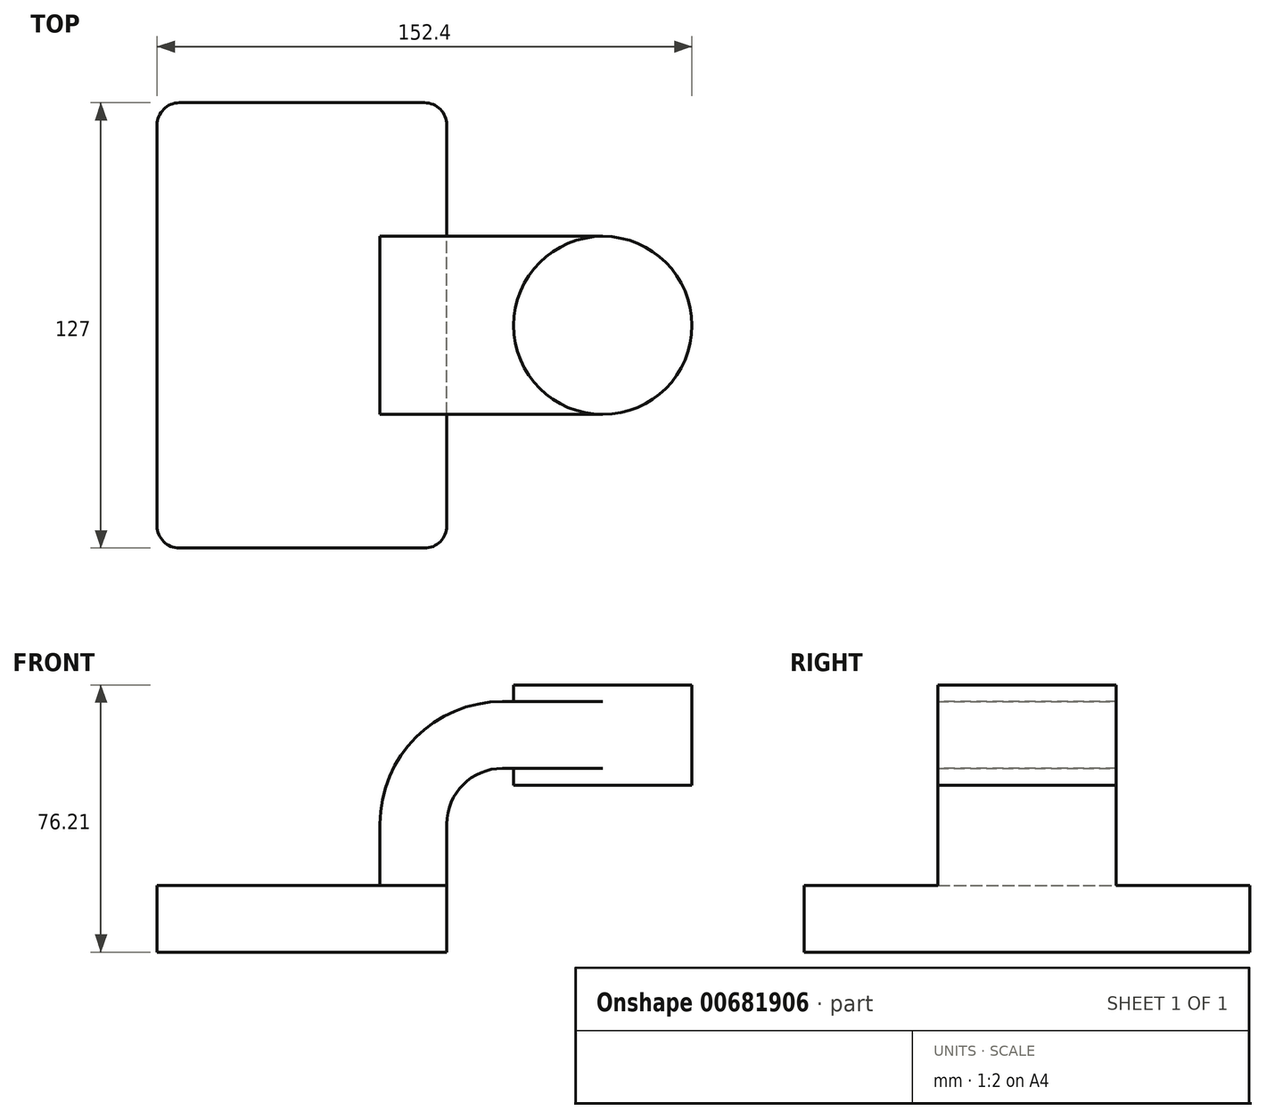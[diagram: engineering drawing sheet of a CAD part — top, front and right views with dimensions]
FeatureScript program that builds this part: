
annotation { "Feature Type Name" : "Feature", "Feature Type Description" : "" }
export const myFeature = defineFeature(function(context is Context, id is Id, definition is map)
    precondition{}
    {
        {
            var Q0;
            Q0=qCreatedBy(makeId("Front.planeOp"),FACE);
            var sketch = newSketch(context, id + "F0", { "sketchPlane" : qUnion([Q0])});
            skLineSegment(sketch, "E0.bottom", {"start": v(-41.28, 9.52) * mm, "end": v(41.27, 9.53) * mm});
            skLineSegment(sketch, "E0.top", {"start": v(-41.28, -9.53) * mm, "end": v(41.28, -9.53) * mm});
            skLineSegment(sketch, "E0.left", {"start": v(-41.28, 9.52) * mm, "end": v(-41.28, -9.53) * mm});
            skLineSegment(sketch, "E0.right", {"start": v(41.27, 9.53) * mm, "end": v(41.28, -9.52) * mm});
            skPoint(sketch, "E0.middle", {"position": v(0, 0) * mm});
            skLineSegment(sketch, "E1.bottom", {"start": v(60.32, 38.1) * mm, "end": v(111.12, 38.1) * mm});
            skLineSegment(sketch, "E1.top", {"start": v(60.32, 66.68) * mm, "end": v(111.12, 66.68) * mm});
            skLineSegment(sketch, "E1.left", {"start": v(60.32, 38.1) * mm, "end": v(60.32, 66.68) * mm});
            skLineSegment(sketch, "E1.right", {"start": v(111.12, 38.1) * mm, "end": v(111.12, 66.68) * mm});
            skPoint(sketch, "E1.middle", {"position": v(85.72, 52.39) * mm});
            skLineSegment(sketch, "E2", {"start": v(41.27, 9.53) * mm, "end": v(41.27, 27) * mm});
            skArc(sketch, "E3", {"start": v(41.27, 27) * mm, "mid": v(45.92, 38.23) * mm, "end": v(57.15, 42.88) * mm});
            skLineSegment(sketch, "E4", {"start": v(57.15, 42.88) * mm, "end": v(85.73, 42.88) * mm});
            skLineSegment(sketch, "E5.0", {"start": v(57.15, 61.93) * mm, "end": v(85.73, 61.93) * mm});
            skArc(sketch, "E5.1", {"start": v(22.22, 27) * mm, "mid": v(32.45, 51.7) * mm, "end": v(57.15, 61.93) * mm});
            skLineSegment(sketch, "E5.2", {"start": v(22.22, 9.53) * mm, "end": v(22.22, 27) * mm});
            skLineSegment(sketch, "E6", {"start": v(85.73, 66.68) * mm, "end": v(85.73, 38.1) * mm});
            skFitSpline(sketch, "E7", {"points": [v(-41.28, 9.53) * mm, v(57.15, 61.93) * mm], "startDerivative": vector(2.17, 103.8) * mm, "endDerivative": vector(152.8, -3.63) * mm});
            skSolve(sketch);
        }
        {
            var Q0;
            Q0=makeQuery(id+"F0.imprint","IMPRINT",FACE,{"disambiguationData":[TD([[makeQuery(id+"F0.imprint","IMPRINT",EDGE,{"derivedFrom":sQuery(id+"F0.wireOp",EDGE,"E0.top")}),1.0]])]});
            extrude(context, id + "F1", {"entities" : qUnion([Q0]), "depth" : 127 * mm, "offsetDistance" : 25.4 * mm, "symmetric" : true});
        }
        {
            var Q0;
            {var subQ1=sQuery(id+"F0.wireOp",EDGE,"E2");Q0=makeQuery(id+"F0.imprint","IMPRINT",FACE,{"disambiguationData":[TD([[makeQuery(id+"F0.imprint","IMPRINT",EDGE,{"derivedFrom":subQ1}),1.0]])]});}
            var Q1;
            {var subQ0=sQuery(id+"F0.wireOp",EDGE,"E4");var subQ1=sQuery(id+"F0.wireOp",EDGE,"E1.left");var subQ2=makeQuery(id+"F0.imprint","INTERSECT",VERTEX,{"derivedFrom":[subQ1,subQ0]});Q1=makeQuery(id+"F0.imprint","IMPRINT",FACE,{"disambiguationData":[TD([[makeQuery(id+"F0.imprint","IMPRINT",EDGE,{"disambiguationData":[TD([[subQ2,-1.0]])],"derivedFrom":subQ1}),-1.0]])]});}
            extrude(context, id + "F2", {"entities" : qUnion([Q0, Q1]), "operationType" : NewBodyOperationType.ADD, "depth" : 50.8 * mm, "offsetDistance" : 25.4 * mm, "symmetric" : true});
        }
        {
            var Q0;
            Q0=makeQuery(id+"F0.imprint","IMPRINT",FACE,{"disambiguationData":[TD([[makeQuery(id+"F0.imprint","IMPRINT",EDGE,{"derivedFrom":sQuery(id+"F0.wireOp",EDGE,"E5.1")}),1.0]])]});
            extrude(context, id + "F3", {"entities" : qUnion([Q0]), "operationType" : NewBodyOperationType.ADD, "depth" : 15.88 * mm, "offsetDistance" : 25.4 * mm, "symmetric" : true});
        }
        {
            var Q0;
            {var subQ0=sQuery(id+"F0.wireOp",EDGE,"E1.right");Q0=makeQuery(id+"F0.imprint","IMPRINT",FACE,{"disambiguationData":[TD([[makeQuery(id+"F0.imprint","IMPRINT",EDGE,{"derivedFrom":subQ0}),1.0]])]});}
            var Q1;
            Q1=sQuery(id+"F0.wireOp",EDGE,"E6");
            revolve(context, id + "F4", {"operationType" : NewBodyOperationType.ADD, "entities" : qUnion([Q0]), "axis" : qUnion([Q1]), "revolveType" : RevolveType.FULL});
        }
        {
            var Q0;
            Q0=makeQuery(id+"F1.opExtrude","CAP_EDGE",EDGE,{"disambiguationData":[OSD([sQuery(id+"F0.wireOp",EDGE,"E0.left")])],"isStart":false});
            var Q1;
            Q1=makeQuery(id+"F1.opExtrude","CAP_EDGE",EDGE,{"disambiguationData":[OSD([sQuery(id+"F0.wireOp",EDGE,"E0.right")])],"isStart":false});
            var Q2;
            Q2=makeQuery(id+"F1.opExtrude","CAP_EDGE",EDGE,{"disambiguationData":[OSD([sQuery(id+"F0.wireOp",EDGE,"E0.right")])],"isStart":true});
            var Q3;
            Q3=makeQuery(id+"F1.opExtrude","CAP_EDGE",EDGE,{"disambiguationData":[OSD([sQuery(id+"F0.wireOp",EDGE,"E0.left")])],"isStart":true});
            fillet(context, id + "F5", {"entities" : qUnion([Q0, Q1, Q2, Q3]), "radius" : 6.35 * mm, "tangentPropagation" : true, "allowEdgeOverflow" : false});
        }
    });
